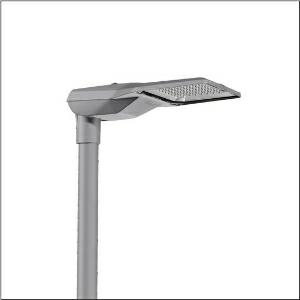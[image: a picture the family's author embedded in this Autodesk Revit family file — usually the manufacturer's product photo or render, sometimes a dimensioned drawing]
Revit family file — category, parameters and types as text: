
# Revit family: streetlight_sl_21_midi___st0_8a_5xe3c33s08nb_db16
name_source: partatom
category: Lighting Fixtures
units: mm (PartAtom-declared; Revit-internal decimal feet)

## family parameters
Cut with Voids When Loaded = No
Host = Face
Light Source = No
Part Type = Normal
Room Calculation Point = No
Round Connector Dimension = Use Diameter
Shared = No

## types (1)
- --- (1 x LED, 22700 lm, 151.2 W, 3000K)
    Apparent Load = 151 VA
    CIE Flux Codes = 41 75 97 100 100
    Color Rendering = 70
    Color Temperature = 3000K
    Default Elevation = 1800 mm
    Description = Streetlight SL 21 midi, mast luminaire, primary light control with lens, of PMMA, primary optical cover: cover, of toughened safety glass, transparent, light distribution: ST0.8a, light emission: direct distribution, primary light characteristic: asymmetric, installation type: side-entry, post-top, LED, High Power LED, rated luminous flux: 22.700lm, luminous efficacy: 150lm/W, light colour: 730, colour temperature: 3000K, control gear: D4i, control: overheat protection, constant luminous flux control, time-dependent luminous flux control, flexible luminous flux parameterisation, pre-setting: logarithmic dimming characteristic, mains connection: 230..240V, AC, 50/60Hz, start of lifetime: 151W, end of service life: 157W, reduction: 70W, luminaire housing, of diecast aluminium, powder-coated, Siteco® metallic grey (DB 702S), corrosivity category C5 mid according to DIN EN ISO 12944, please order mast flange separately, inclination adjustable: 0°, 5°, 10°, 15°, sealing non-destructively replaceable, multi-level sealing system, length: 644mm, width: 335mm, height: 110mm, mast flange for spigot size: 42mm (side-entry): 5XC10008XM4, 60/48mm (side-entry/post-top): 5XC10108XM2, 76/60mm (side-entry/post-top): 5XC10108XM1, mounting height: 4..8m, Smart Interface above, protection rating (complete): IP66, insulation class (complete): insulation class II (safety insulation), certification: CE, ENEC, ENEC+, VDE, impact resistance: IK10, permissible operating ambient temperature for outdoor applications: -40..+50°C, standard-compliant lighting for roads and squares, packaging unit: 1 piece

Light Distribution: ST0.8a
    Height = 111 mm
    Lamp = 1 x LED
    Lamp Light Flux = 22700 lm
    Lamp Power = 151.2 W
    Lamp count = 1
    Length = 644 mm
    Luminous efficacy = 150 lm/W
    Manufacturer = Siteco
    ModVariant = No
    Model = 5XE3C33S08NB
    Number of Poles = 1
    OnlyDefault = Yes
    Power Factor = 1
    Product Name = Streetlight SL 21 midi | ST0.8a
    Product group = mast luminaire | pylon top
    ProductGroupID = 6100
    Protection Class = Protection class II
    Protection Degree = IP 66
    RLX_Detail_Level = 1
    RLX_Emergency_Light_Flux = 0 lm
    RLX_Emergency_Type = 0
    RLX_Emergency_Type_DB = No
    RlxData = <blob elided: 26909 chars, md5=52121ae4>
    Socket = socket
    Standby Power = 0 W
    System Light Flux = 22700 lm
    System Power = 151 W
    Type Comments = factory setting: luminous flux: 100 % | dim-lin: 254 | 802 mA
    Type Image = l_1004302.jpg
    URL = http://relux.com
    VarID = @adj_190223
    Voltage = 0 V
    Weight = 0.00 kg
    Width = 336 mm

## geometry (parser evidence)
native form markers: Blend x4, Sweep x13
no freeform markers — native parametric forms only
